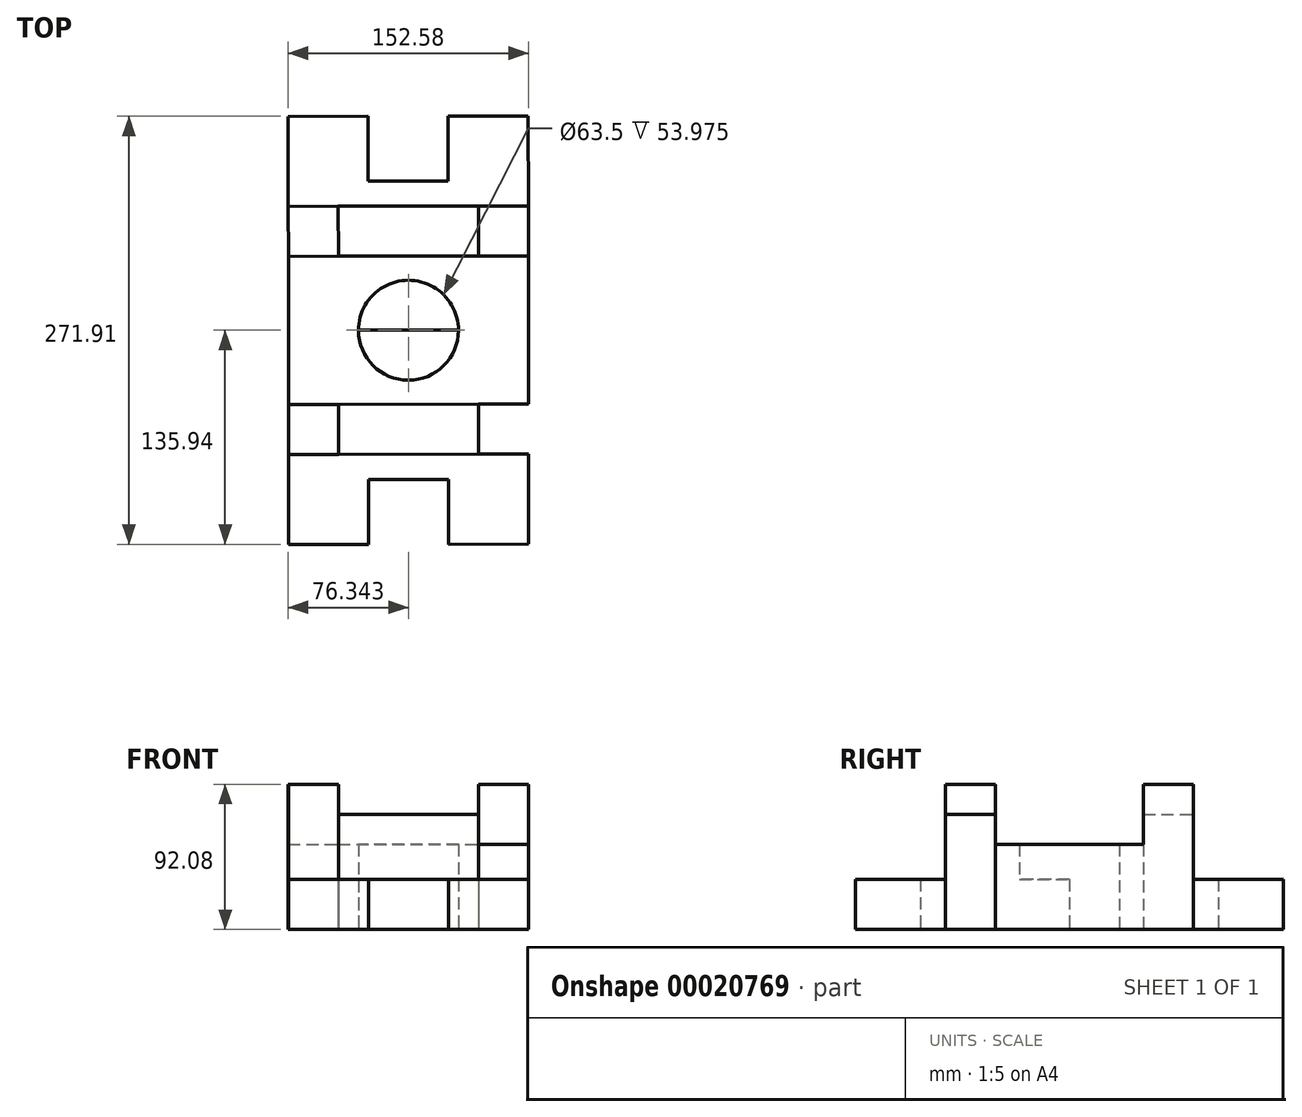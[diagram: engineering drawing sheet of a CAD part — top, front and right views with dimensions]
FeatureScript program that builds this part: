
annotation { "Feature Type Name" : "Feature", "Feature Type Description" : "" }
export const myFeature = defineFeature(function(context is Context, id is Id, definition is map)
    precondition{}
    {
        {
            var Q0;
            Q0=qCreatedBy(makeId("Top.planeOp"),FACE);
            var sketch = newSketch(context, id + "F0", { "sketchPlane" : qUnion([Q0])});
            skLineSegment(sketch, "E0", {"start": v(-140.16, -58.17) * mm, "end": v(-89.36, -58.17) * mm});
            skLineSegment(sketch, "E1", {"start": v(-89.36, -58.17) * mm, "end": v(-89.36, -16.9) * mm});
            skLineSegment(sketch, "E2", {"start": v(-89.36, -16.9) * mm, "end": v(-38.56, -16.9) * mm});
            skLineSegment(sketch, "E3", {"start": v(-38.56, -16.9) * mm, "end": v(-38.56, -58.17) * mm});
            skLineSegment(sketch, "E4", {"start": v(-38.56, -58.17) * mm, "end": v(12.24, -58.08) * mm});
            skLineSegment(sketch, "E5", {"start": v(12.26, -0.93) * mm, "end": v(12.24, -58.08) * mm});
            skLineSegment(sketch, "E6", {"start": v(-140.17, -1.02) * mm, "end": v(12.26, -0.93) * mm});
            skLineSegment(sketch, "E7", {"start": v(-140.17, -1.02) * mm, "end": v(-140.16, -58.17) * mm});
            skLineSegment(sketch, "E8", {"start": v(-19.5, -0.95) * mm, "end": v(12.26, -0.93) * mm});
            skPoint(sketch, "E9.start.orphan", {"position": v(-140.17, 38.35) * mm});
            skPoint(sketch, "E10.start.orphan", {"position": v(12.24, 38.44) * mm});
            skLineSegment(sketch, "E11", {"start": v(-140.18, 30.74) * mm, "end": v(-108.43, 30.74) * mm});
            skLineSegment(sketch, "E12", {"start": v(12.24, 30.82) * mm, "end": v(-19.51, 30.8) * mm});
            skLineSegment(sketch, "E13", {"start": v(-19.51, 30.8) * mm, "end": v(-19.5, -0.95) * mm});
            skLineSegment(sketch, "E14", {"start": v(12.24, 30.82) * mm, "end": v(12.26, -0.93) * mm});
            skLineSegment(sketch, "E15", {"start": v(-108.43, 30.74) * mm, "end": v(-108.43, -1) * mm});
            skLineSegment(sketch, "E16", {"start": v(-140.18, 30.74) * mm, "end": v(-140.17, -1.02) * mm});
            skLineSegment(sketch, "E17", {"start": v(-140.18, 77.73) * mm, "end": v(-140.18, 30.74) * mm});
            skLineSegment(sketch, "E18", {"start": v(12.22, 77.82) * mm, "end": v(12.24, 30.82) * mm});
            skArc(sketch, "E19", {"start": v(-95.73, 77.75) * mm, "mid": v(-63.96, 46.02) * mm, "end": v(-32.23, 77.79) * mm});
            skLineSegment(sketch, "E20", {"start": v(-140.18, 77.73) * mm, "end": v(12.22, 77.82) * mm});
            skLineSegment(sketch, "E21.MirrorCS", {"start": v(-140.18, 77.73) * mm, "end": v(-140.24, 124.71) * mm});
            skLineSegment(sketch, "E22.MirrorCS", {"start": v(-140.24, 124.71) * mm, "end": v(-140.26, 156.47) * mm});
            skLineSegment(sketch, "E23.MirrorCS", {"start": v(-140.26, 156.47) * mm, "end": v(-140.32, 213.62) * mm});
            skArc(sketch, "E24.MirrorCS", {"start": v(-95.73, 77.75) * mm, "mid": v(-64, 109.52) * mm, "end": v(-32.23, 77.79) * mm});
            skLineSegment(sketch, "E25.MirrorCS", {"start": v(-140.26, 156.47) * mm, "end": v(12.16, 156.56) * mm});
            skLineSegment(sketch, "E26.MirrorCS", {"start": v(-108.49, 124.74) * mm, "end": v(-108.52, 156.5) * mm});
            skLineSegment(sketch, "E27.MirrorCS", {"start": v(-140.24, 124.71) * mm, "end": v(-108.49, 124.74) * mm});
            skLineSegment(sketch, "E28.MirrorCS", {"start": v(-19.57, 124.8) * mm, "end": v(-19.59, 156.55) * mm});
            skLineSegment(sketch, "E29.MirrorCS", {"start": v(12.18, 124.81) * mm, "end": v(-19.57, 124.8) * mm});
            skLineSegment(sketch, "E30.MirrorCS", {"start": v(-19.59, 156.55) * mm, "end": v(12.16, 156.56) * mm});
            skLineSegment(sketch, "E31.MirrorCS", {"start": v(12.18, 124.81) * mm, "end": v(12.16, 156.56) * mm});
            skLineSegment(sketch, "E32.MirrorCS", {"start": v(12.16, 156.56) * mm, "end": v(12.08, 213.71) * mm});
            skLineSegment(sketch, "E33.MirrorCS", {"start": v(-38.72, 213.74) * mm, "end": v(12.08, 213.71) * mm});
            skLineSegment(sketch, "E34.MirrorCS", {"start": v(-89.47, 172.4) * mm, "end": v(-38.67, 172.47) * mm});
            skLineSegment(sketch, "E35.MirrorCS", {"start": v(-89.52, 213.68) * mm, "end": v(-89.47, 172.4) * mm});
            skLineSegment(sketch, "E36.MirrorCS", {"start": v(-38.67, 172.47) * mm, "end": v(-38.72, 213.74) * mm});
            skLineSegment(sketch, "E37.MirrorCS", {"start": v(-140.32, 213.62) * mm, "end": v(-89.52, 213.68) * mm});
            skLineSegment(sketch, "E38.MirrorCS", {"start": v(12.22, 77.82) * mm, "end": v(12.18, 124.81) * mm});
            skLineSegment(sketch, "E39", {"start": v(-108.43, 30.74) * mm, "end": v(-19.51, 30.8) * mm});
            skLineSegment(sketch, "E40", {"start": v(-108.49, 124.74) * mm, "end": v(-19.57, 124.8) * mm});
            skSolve(sketch);
        }
        {
            var Q0;
            Q0=makeQuery(id+"F0.imprint","IMPRINT",FACE,{"disambiguationData":[TD([[makeQuery(id+"F0.imprint","IMPRINT",EDGE,{"derivedFrom":sQuery(id+"F0.wireOp",EDGE,"E8")}),1.0]])]});
            var Q1;
            {var subQ2=sQuery(id+"F0.wireOp",EDGE,"E22.MirrorCS");Q1=makeQuery(id+"F0.imprint","IMPRINT",FACE,{"disambiguationData":[TD([[makeQuery(id+"F0.imprint","IMPRINT",EDGE,{"derivedFrom":subQ2}),-1.0]])]});}
            var Q2;
            Q2=makeQuery(id+"F0.imprint","IMPRINT",FACE,{"disambiguationData":[TD([[makeQuery(id+"F0.imprint","IMPRINT",EDGE,{"derivedFrom":sQuery(id+"F0.wireOp",EDGE,"E28.MirrorCS")}),-1.0]])]});
            var Q3;
            Q3=makeQuery(id+"F0.imprint","IMPRINT",FACE,{"disambiguationData":[TD([[makeQuery(id+"F0.imprint","IMPRINT",EDGE,{"derivedFrom":sQuery(id+"F0.wireOp",EDGE,"E11")}),-1.0]])]});
            extrude(context, id + "F1", {"entities" : qUnion([Q0, Q1, Q2, Q3]), "depth" : 92.07 * mm});
        }
        {
            var Q0;
            Q0=makeQuery(id+"F0.imprint","IMPRINT",FACE,{"disambiguationData":[TD([[makeQuery(id+"F0.imprint","IMPRINT",EDGE,{"derivedFrom":sQuery(id+"F0.wireOp",EDGE,"E0")}),1.0]])]});
            var Q1;
            {var subQ3=sQuery(id+"F0.wireOp",EDGE,"E23.MirrorCS");Q1=makeQuery(id+"F0.imprint","IMPRINT",FACE,{"disambiguationData":[TD([[makeQuery(id+"F0.imprint","IMPRINT",EDGE,{"derivedFrom":subQ3}),-1.0]])]});}
            extrude(context, id + "F2", {"entities" : qUnion([Q0, Q1]), "depth" : 31.75 * mm});
        }
        {
            var Q0;
            {var subQ2=sQuery(id+"F0.wireOp",EDGE,"E21.MirrorCS");Q0=makeQuery(id+"F0.imprint","IMPRINT",FACE,{"disambiguationData":[TD([[makeQuery(id+"F0.imprint","IMPRINT",EDGE,{"derivedFrom":subQ2}),-1.0]])]});}
            var Q1;
            Q1=makeQuery(id+"F0.imprint","IMPRINT",FACE,{"disambiguationData":[TD([[makeQuery(id+"F0.imprint","IMPRINT",EDGE,{"derivedFrom":sQuery(id+"F0.wireOp",EDGE,"E11")}),1.0]])]});
            extrude(context, id + "F3", {"entities" : qUnion([Q0, Q1]), "depth" : 53.97 * mm});
        }
        {
            var Q0;
            {var subQ0=sQuery(id+"F0.wireOp",EDGE,"E24.MirrorCS");Q0=makeQuery(id+"F0.imprint","IMPRINT",FACE,{"disambiguationData":[TD([[makeQuery(id+"F0.imprint","IMPRINT",EDGE,{"derivedFrom":subQ0}),-1.0]])]});}
            var Q1;
            {var subQ1=sQuery(id+"F0.wireOp",EDGE,"E19");Q1=makeQuery(id+"F0.imprint","IMPRINT",FACE,{"disambiguationData":[TD([[makeQuery(id+"F0.imprint","IMPRINT",EDGE,{"derivedFrom":subQ1}),1.0]])]});}
            extrude(context, id + "F4", {"entities" : qUnion([Q0, Q1]), "operationType" : NewBodyOperationType.ADD, "depth" : 31.75 * mm});
        }
        {
            var Q0;
            {var subQ1=sQuery(id+"F0.wireOp",EDGE,"E13");Q0=makeQuery(id+"F0.imprint","IMPRINT",FACE,{"disambiguationData":[TD([[makeQuery(id+"F0.imprint","IMPRINT",EDGE,{"derivedFrom":subQ1}),-1.0]])]});}
            var Q1;
            {var subQ1=sQuery(id+"F0.wireOp",EDGE,"E26.MirrorCS");Q1=makeQuery(id+"F0.imprint","IMPRINT",FACE,{"disambiguationData":[TD([[makeQuery(id+"F0.imprint","IMPRINT",EDGE,{"derivedFrom":subQ1}),-1.0]])]});}
            extrude(context, id + "F5", {"entities" : qUnion([Q0, Q1]), "depth" : 73.02 * mm});
        }
    });
